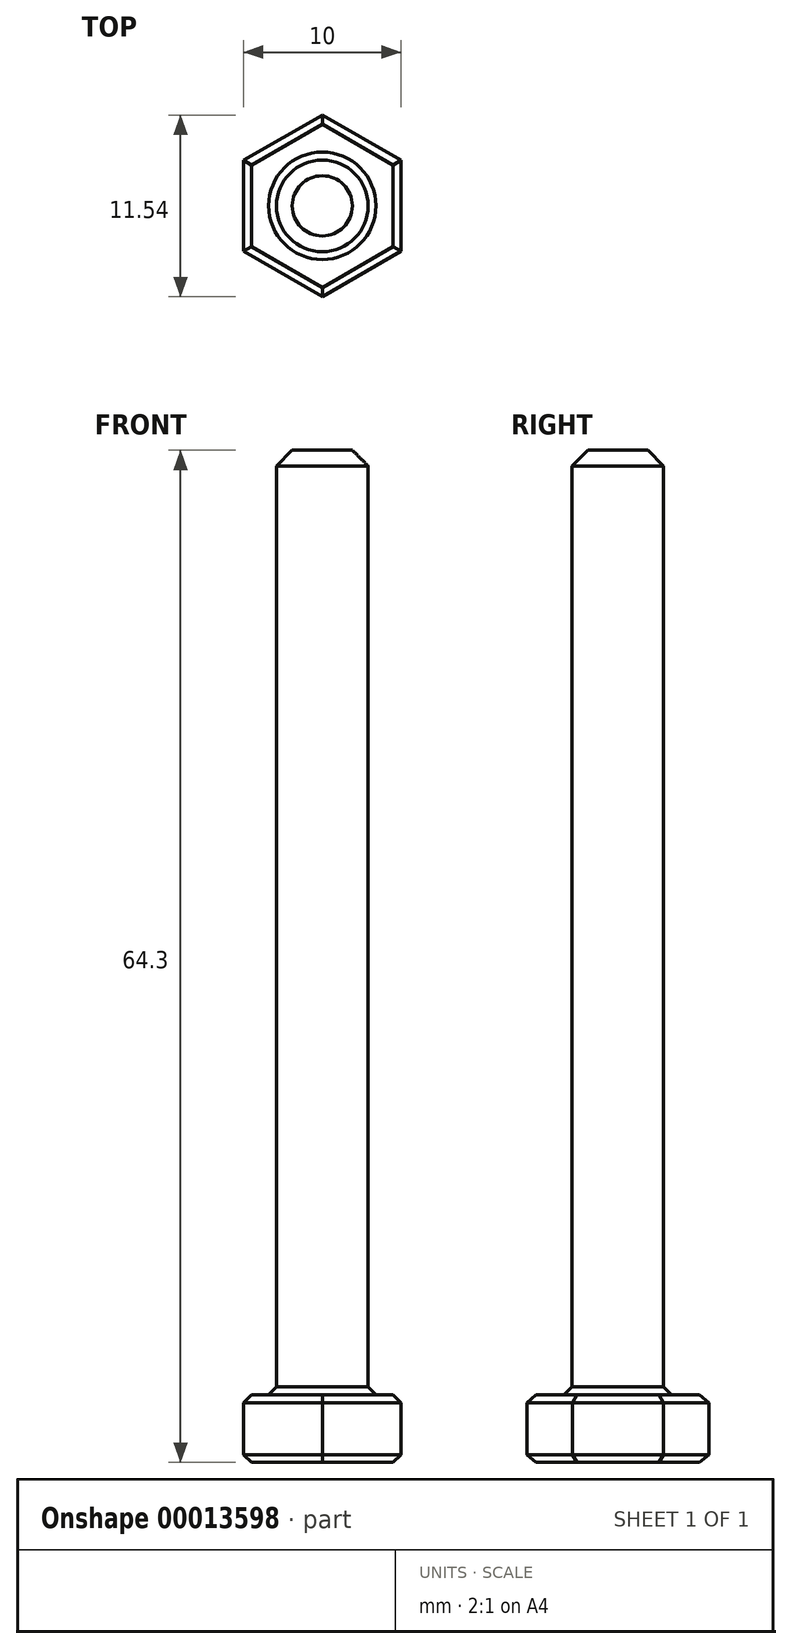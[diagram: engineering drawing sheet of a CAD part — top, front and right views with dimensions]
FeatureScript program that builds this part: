
annotation { "Feature Type Name" : "Feature", "Feature Type Description" : "" }
export const myFeature = defineFeature(function(context is Context, id is Id, definition is map)
    precondition{}
    {
        {
            var Q0;
            Q0=qCreatedBy(makeId("Top.planeOp"),FACE);
            var sketch = newSketch(context, id + "F0", { "sketchPlane" : qUnion([Q0])});
            skCircle(sketch, "E0.cCircle", {"center": v(0, 0) * mm, "radius": 5 * mm, "construction": true});
            skLineSegment(sketch, "E0.0", {"start": v(5, 2.89) * mm, "end": v(5, -2.89) * mm});
            skLineSegment(sketch, "E0.1", {"start": v(5, -2.89) * mm, "end": v(0, -5.77) * mm});
            skLineSegment(sketch, "E0.2", {"start": v(0, -5.77) * mm, "end": v(-5, -2.89) * mm});
            skLineSegment(sketch, "E0.3", {"start": v(-5, -2.89) * mm, "end": v(-5, 2.89) * mm});
            skLineSegment(sketch, "E0.4", {"start": v(-5, 2.89) * mm, "end": v(0, 5.77) * mm});
            skLineSegment(sketch, "E0.5", {"start": v(0, 5.77) * mm, "end": v(5, 2.89) * mm});
            skPoint(sketch, "E0.0.midPoint", {"position": v(5, 0) * mm});
            skCircle(sketch, "E1", {"center": v(0, 0) * mm, "radius": 2.91 * mm});
            skSolve(sketch);
        }
        {
            var Q0;
            Q0=makeQuery(id+"F0.imprint","IMPRINT",FACE,{"disambiguationData":[TD([[makeQuery(id+"F0.imprint","IMPRINT",EDGE,{"derivedFrom":sQuery(id+"F0.wireOp",EDGE,"E0.0")}),-1.0]])]});
            var Q1;
            Q1=makeQuery(id+"F0.imprint","IMPRINT",FACE,{"disambiguationData":[TD([[makeQuery(id+"F0.imprint","IMPRINT",EDGE,{"derivedFrom":sQuery(id+"F0.wireOp",EDGE,"E1")}),1.0]])]});
            extrude(context, id + "F1", {"entities" : qUnion([Q0, Q1]), "oppositeDirection" : true, "depth" : 4.3 * mm});
        }
        {
            var Q0;
            Q0=makeQuery(id+"F0.imprint","IMPRINT",FACE,{"disambiguationData":[TD([[makeQuery(id+"F0.imprint","IMPRINT",EDGE,{"derivedFrom":sQuery(id+"F0.wireOp",EDGE,"E1")}),1.0]])]});
            extrude(context, id + "F2", {"entities" : qUnion([Q0]), "operationType" : NewBodyOperationType.ADD, "depth" : 60 * mm});
        }
        {
            var Q0;
            Q0=makeQuery(id+"F2.opExtrude","CAP_EDGE",EDGE,{"disambiguationData":[OSD([sQuery(id+"F0.wireOp",EDGE,"E1")])],"isStart":false});
            chamfer(context, id + "F3", {"entities" : qUnion([Q0]), "width" : 1 * mm, "tangentPropagation" : true});
        }
        {
            var Q0;
            Q0=makeQuery(id+"F1.opExtrude","CAP_FACE",FACE,{"disambiguationData":[OSD([sQuery(id+"F0.wireOp",EDGE,"E0.0"),sQuery(id+"F0.wireOp",EDGE,"E0.1"),sQuery(id+"F0.wireOp",EDGE,"E0.2"),sQuery(id+"F0.wireOp",EDGE,"E0.3"),sQuery(id+"F0.wireOp",EDGE,"E0.4"),sQuery(id+"F0.wireOp",EDGE,"E0.5")])],"isStart":false});
            var Q1;
            Q1=makeQuery(id+"F1.opExtrude","CAP_FACE",FACE,{"disambiguationData":[OSD([sQuery(id+"F0.wireOp",EDGE,"E0.0"),sQuery(id+"F0.wireOp",EDGE,"E0.1"),sQuery(id+"F0.wireOp",EDGE,"E0.2"),sQuery(id+"F0.wireOp",EDGE,"E0.3"),sQuery(id+"F0.wireOp",EDGE,"E0.4"),sQuery(id+"F0.wireOp",EDGE,"E0.5")])],"isStart":true});
            chamfer(context, id + "F4", {"entities" : qUnion([Q0, Q1]), "width" : 0.5 * mm, "tangentPropagation" : true});
        }
    });
